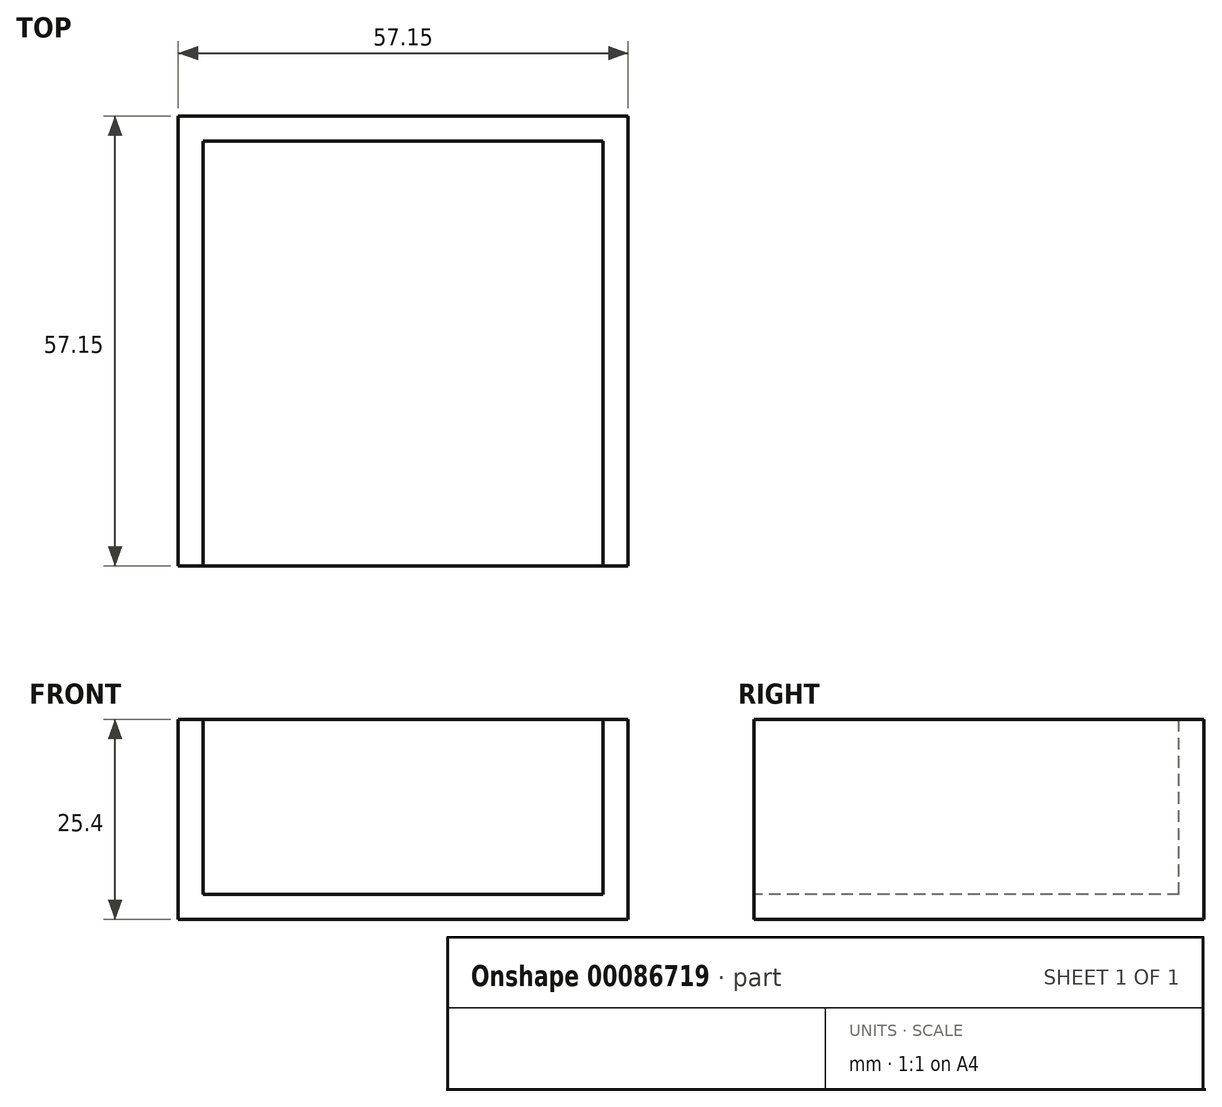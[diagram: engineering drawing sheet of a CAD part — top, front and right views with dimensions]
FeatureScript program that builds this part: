
annotation { "Feature Type Name" : "Feature", "Feature Type Description" : "" }
export const myFeature = defineFeature(function(context is Context, id is Id, definition is map)
    precondition{}
    {
        {
            var Q0;
            Q0=qCreatedBy(makeId("Top.planeOp"),FACE);
            var sketch = newSketch(context, id + "F0", { "sketchPlane" : qUnion([Q0])});
            skLineSegment(sketch, "E0.bottom", {"start": v(-57.15, 57.15) * mm, "end": v(0, 57.15) * mm});
            skLineSegment(sketch, "E0.top", {"start": v(-57.15, 0) * mm, "end": v(0, 0) * mm});
            skLineSegment(sketch, "E0.left", {"start": v(-57.15, 57.15) * mm, "end": v(-57.15, 0) * mm});
            skLineSegment(sketch, "E0.right", {"start": v(0, 57.15) * mm, "end": v(0, 0) * mm});
            skSolve(sketch);
        }
        {
            var Q0;
            Q0=makeQuery(id+"F0.imprint","IMPRINT",FACE,{"disambiguationData":[TD([[makeQuery(id+"F0.imprint","IMPRINT",EDGE,{"derivedFrom":sQuery(id+"F0.wireOp",EDGE,"E0.bottom")}),-1.0]])]});
            extrude(context, id + "F1", {"entities" : qUnion([Q0]), "depth" : 25.4 * mm});
        }
        {
            var Q0;
            Q0=makeQuery(id+"F1.opExtrude","CAP_FACE",FACE,{"disambiguationData":[OSD([sQuery(id+"F0.wireOp",EDGE,"E0.bottom"),sQuery(id+"F0.wireOp",EDGE,"E0.top"),sQuery(id+"F0.wireOp",EDGE,"E0.left"),sQuery(id+"F0.wireOp",EDGE,"E0.right")])],"isStart":false});
            var sketch = newSketch(context, id + "F2", { "sketchPlane" : qUnion([Q0])});
            skLineSegment(sketch, "E1.bottom", {"start": v(-53.98, 53.98) * mm, "end": v(-3.18, 53.98) * mm});
            skLineSegment(sketch, "E1.top", {"start": v(-53.98, 0) * mm, "end": v(-3.18, 0) * mm});
            skLineSegment(sketch, "E1.left", {"start": v(-53.98, 53.98) * mm, "end": v(-53.98, 0) * mm});
            skLineSegment(sketch, "E1.right", {"start": v(-3.18, 53.98) * mm, "end": v(-3.18, 0) * mm});
            skLineSegment(sketch, "E2", {"start": v(-57.15, 57.15) * mm, "end": v(-53.98, 57.15) * mm});
            skLineSegment(sketch, "E3", {"start": v(-53.98, 57.15) * mm, "end": v(-53.98, 53.98) * mm});
            skSolve(sketch);
        }
        {
            var Q0;
            Q0 = qSketchRegion(id + "F2", true);
            extrude(context, id + "F3", {"entities" : qUnion([Q0]), "operationType" : NewBodyOperationType.REMOVE, "oppositeDirection" : true, "depth" : 22.22 * mm});
        }
    });
